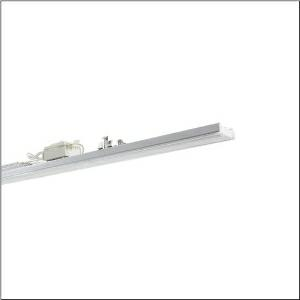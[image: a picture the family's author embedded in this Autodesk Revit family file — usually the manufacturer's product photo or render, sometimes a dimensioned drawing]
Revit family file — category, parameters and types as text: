
# Revit family: licross_11_recessed_mo_51tl147n48xg
name_source: partatom
category: Lighting Fixtures
units: mm (PartAtom-declared; Revit-internal decimal feet)

## family parameters
Cut with Voids When Loaded = No
Host = Face
Light Source = No
Part Type = Normal
Room Calculation Point = No
Round Connector Dimension = Use Diameter
Shared = No

## types (1)
- Licross 11 Recessed MO (1 x LED, 8240 lm, 48.5 W, 4000K)
    Apparent Load = 49 VA
    CIE Flux Codes = 56 84 97 100 100
    Color Rendering = 80
    Color Temperature = 4000K
    Default Elevation = 1800 mm
    Description = Licross 11 Recessed MO, luminaire insert, of sheet steel, coil coated, white, length: 1.500mm, width: 66mm, height: 67mm, LED rated luminous flux: 8.240lm, light colour: 840, SDCM (Standard Deviation of Colour Matching)MacAdam ≤ 2 SDCM (initial), control gear: ON/OFF, with plug, 3-pole, with phase selection, mains connection: 220..240V, AC, 50/60Hz, rated input power: 49W, internal wiring halogen-free, primary light control with lens, of plastic, primary optical cover: cover, of PMMA, light emission: direct distribution, primary light characteristic: asymmetric, protection rating (complete): IP40, insulation class (complete): insulation class I (protective earthing), certification: CE, ENEC, VDE, UKCA, protection symbol: D if used in an environment without relevant dust loads with corresponding accessories, impact resistance: IK06, permissible ambient temperature for indoor applications: -35..+35°C, corresponds to IFS (International Featured Standards) requirements for safety and quality in the food industry, reducing of maximum allowable ambient temperature of 5°C with ceiling mounting, The light source and the operating device comply with the requirements of the Ecodesign Regulation (EU) 2019/2020 and are replaceable in accordance with this regulation, packaging unit: 1 piece
    Height = 58 mm
    Lamp = 1 x LED
    Lamp Light Flux = 8240 lm
    Lamp Power = 48.5 W
    Lamp count = 1
    Length = 1500 mm
    Luminous efficacy = 170 lm/W
    Manufacturer = Siteco
    ModVariant = No
    Model = 51TL147N48XG
    Mounting Place = Ceiling
    Mounting Type = Pendant
    Number of Poles = 1
    OnlyDefault = Yes
    Power Factor = 1
    Product Name = Licross 11 Recessed MO
    Product group = luminaire insert | ceiling pendant
    ProductGroupID = 901
    Protection Class = Protection class I
    Protection Degree = IP 40
    RLX_Detail_Level = 1
    RLX_Emergency_Light_Flux = 0 lm
    RLX_Emergency_Type = 0
    RLX_Emergency_Type_DB = No
    RlxData = <blob elided: 21577 chars, md5=cedc225d>
    Socket = socket
    Standby Power = 0 W
    System Light Flux = 8240 lm
    System Power = 49 W
    Type Comments = Product without accessories
    Type Image = l_1296930.jpg
    URL = http://relux.com
    VarID = ---
    Voltage = 0 V
    Weight = 0.00 kg
    Width = 66 mm

## geometry (parser evidence)
native form markers: Blend x4, Sweep x10
no freeform markers — native parametric forms only
